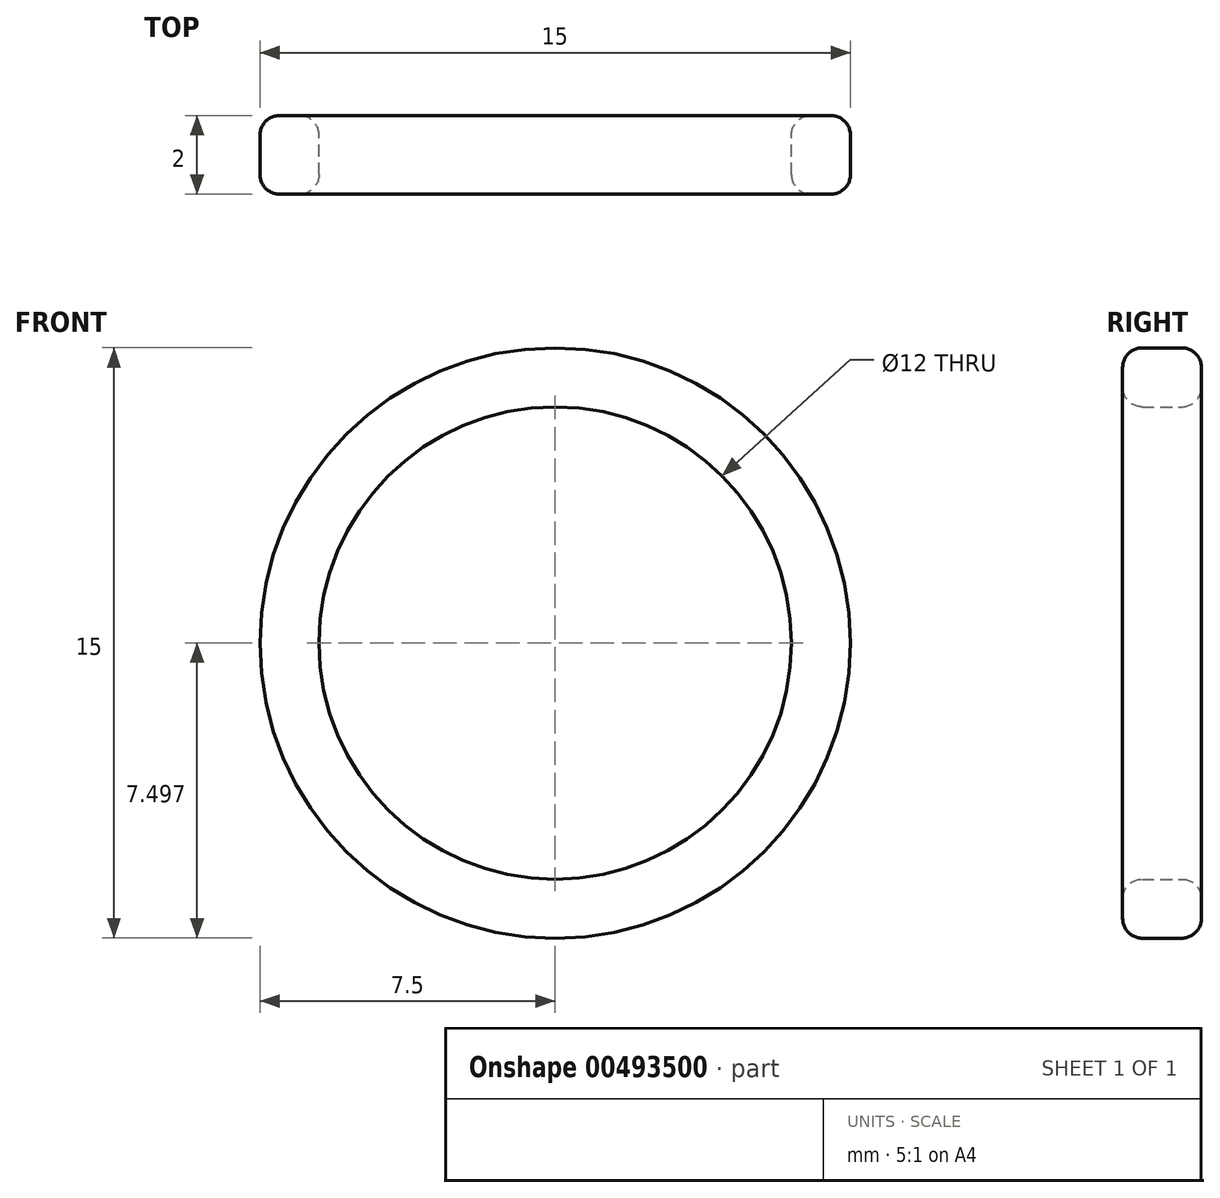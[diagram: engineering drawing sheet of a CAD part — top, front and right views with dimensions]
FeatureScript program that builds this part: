
annotation { "Feature Type Name" : "Feature", "Feature Type Description" : "" }
export const myFeature = defineFeature(function(context is Context, id is Id, definition is map)
    precondition{}
    {
        {
            var Q0;
            Q0=qCreatedBy(makeId("Front.planeOp"),FACE);
            var sketch = newSketch(context, id + "F0", { "sketchPlane" : qUnion([Q0])});
            skCircle(sketch, "E0", {"center": v(0, 0) * mm, "radius": 8.9 * mm});
            skCircle(sketch, "E1", {"center": v(0, 19.94) * mm, "radius": 9.6 * mm});
            skCircle(sketch, "E2", {"center": v(0, 43.53) * mm, "radius": 6.7 * mm});
            skCircle(sketch, "E3", {"center": v(0, 69.45) * mm, "radius": 9.42 * mm});
            skCircle(sketch, "E4", {"center": v(0, 92.68) * mm, "radius": 6 * mm});
            skCircle(sketch, "E5", {"center": v(0, 113.1) * mm, "radius": 6 * mm});
            skCircle(sketch, "E6", {"center": v(0, 92.68) * mm, "radius": 7.5 * mm});
            skSolve(sketch);
        }
        {
            var Q0;
            Q0=makeQuery(id+"F0.imprint","IMPRINT",FACE,{"disambiguationData":[TD([[makeQuery(id+"F0.imprint","IMPRINT",EDGE,{"derivedFrom":sQuery(id+"F0.wireOp",EDGE,"E4")}),-1.0]])]});
            extrude(context, id + "F1", {"entities" : qUnion([Q0]), "depth" : 2 * mm});
        }
        {
            var Q0;
            Q0=makeQuery(id+"F1.opExtrude","CAP_FACE",FACE,{"disambiguationData":[OSD([sQuery(id+"F0.wireOp",EDGE,"E4"),sQuery(id+"F0.wireOp",EDGE,"E6")])],"isStart":false});
            var Q1;
            Q1=makeQuery(id+"F1.opExtrude","CAP_EDGE",EDGE,{"disambiguationData":[OSD([sQuery(id+"F0.wireOp",EDGE,"E6")])],"isStart":true});
            var Q2;
            Q2=makeQuery(id+"F1.opExtrude","CAP_EDGE",EDGE,{"disambiguationData":[OSD([sQuery(id+"F0.wireOp",EDGE,"E6")])],"isStart":false});
            var Q3;
            Q3=makeQuery(id+"F1.opExtrude","CAP_EDGE",EDGE,{"disambiguationData":[OSD([sQuery(id+"F0.wireOp",EDGE,"E4")])],"isStart":false});
            var Q4;
            Q4=makeQuery(id+"F1.opExtrude","CAP_EDGE",EDGE,{"disambiguationData":[OSD([sQuery(id+"F0.wireOp",EDGE,"E4")])],"isStart":true});
            var Q5;
            Q5=makeQuery(id+"F1.opExtrude","CAP_FACE",FACE,{"disambiguationData":[OSD([sQuery(id+"F0.wireOp",EDGE,"E4"),sQuery(id+"F0.wireOp",EDGE,"E6")])],"isStart":true});
            fillet(context, id + "F2", {"entities" : qUnion([Q0, Q1, Q2, Q3, Q4, Q5]), "radius" : .5 * mm, "tangentPropagation" : true, "allowEdgeOverflow" : false});
        }
        {
            var Q0;
            Q0=sQuery(id+"F0.wireOp",EDGE,"E5");
            var Q1;
            Q1=sQuery(id+"F0.wireOp",EDGE,"E4");
            var Q2;
            Q2=sQuery(id+"F0.wireOp",EDGE,"E3");
            var Q3;
            Q3=sQuery(id+"F0.wireOp",EDGE,"E2");
            var Q4;
            Q4=sQuery(id+"F0.wireOp",EDGE,"E1");
            var Q5;
            Q5=sQuery(id+"F0.wireOp",EDGE,"E0");
            extrude(context, id + "F3", {"bodyType" : ToolBodyType.SURFACE, "surfaceEntities" : qUnion([Q0, Q1, Q2, Q3, Q4, Q5]), "depth" : 2.3 * mm});
        }
    });
